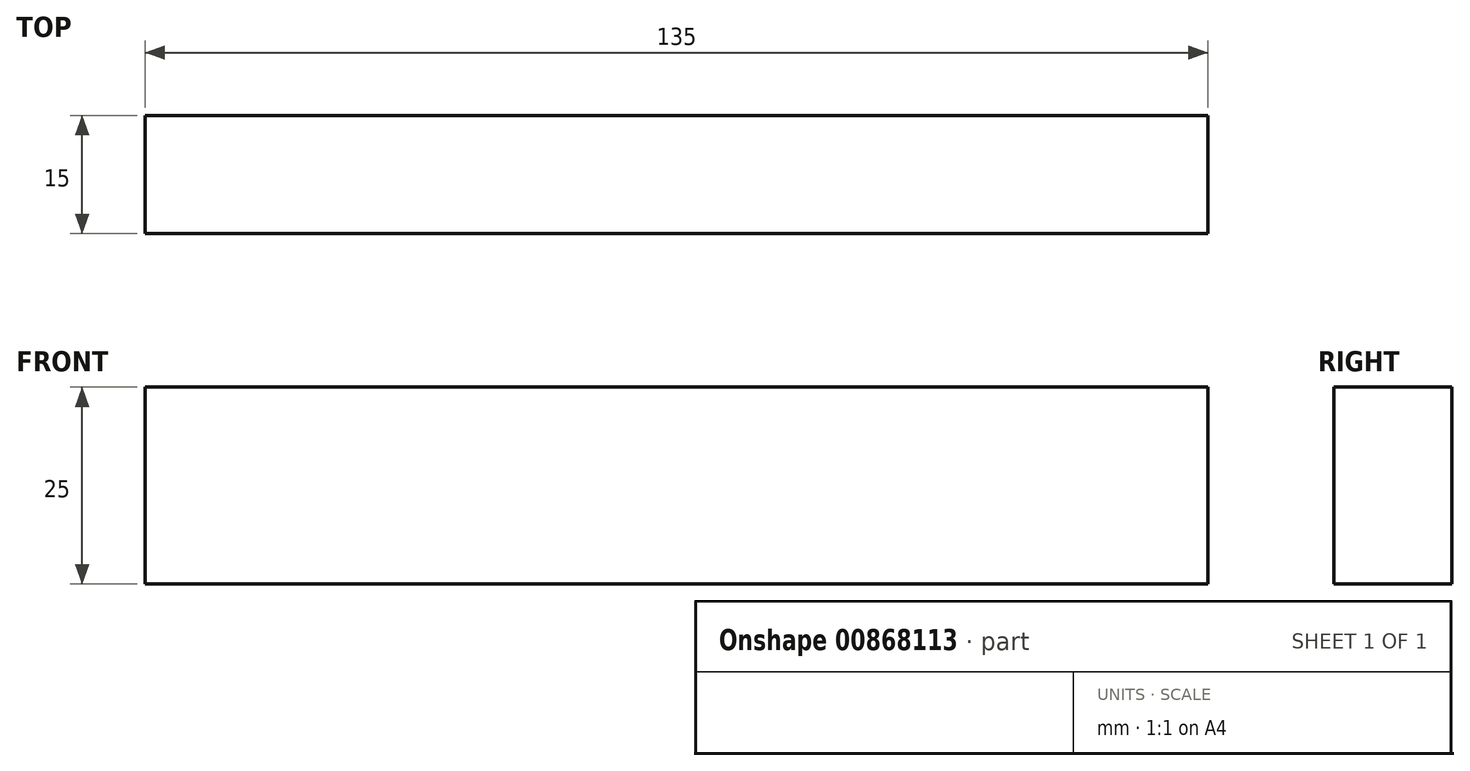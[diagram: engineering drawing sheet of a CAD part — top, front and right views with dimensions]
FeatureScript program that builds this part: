
annotation { "Feature Type Name" : "Feature", "Feature Type Description" : "" }
export const myFeature = defineFeature(function(context is Context, id is Id, definition is map)
    precondition{}
    {
        {
            var Q0;
            Q0=qCreatedBy(makeId("Front.planeOp"),FACE);
            var sketch = newSketch(context, id + "F0", { "sketchPlane" : qUnion([Q0])});
            skLineSegment(sketch, "E0.bottom", {"start": v(-46.7, 23.1) * mm, "end": v(88.3, 23.1) * mm});
            skLineSegment(sketch, "E0.top", {"start": v(-46.7, -1.9) * mm, "end": v(88.3, -1.9) * mm});
            skLineSegment(sketch, "E0.left", {"start": v(-46.7, 23.1) * mm, "end": v(-46.7, -1.9) * mm});
            skLineSegment(sketch, "E0.right", {"start": v(88.3, 23.1) * mm, "end": v(88.3, -1.9) * mm});
            skSolve(sketch);
        }
        {
            var Q0;
            Q0 = qSketchRegion(id + "F0", true);
            extrude(context, id + "F1", {"entities" : qUnion([Q0]), "depth" : 15 * mm, "offsetDistance" : 25 * mm});
        }
    });
